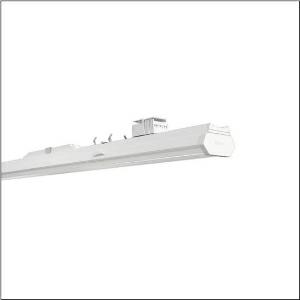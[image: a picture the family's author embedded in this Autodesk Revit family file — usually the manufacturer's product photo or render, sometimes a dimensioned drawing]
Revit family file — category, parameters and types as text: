
# Revit family: licross_11_protected_mo_51tp12dn495g3s4
name_source: partatom
category: Lighting Fixtures
units: mm (PartAtom-declared; Revit-internal decimal feet)

## family parameters
Cut with Voids When Loaded = No
Host = Face
Light Source = No
Part Type = Normal
Room Calculation Point = No
Round Connector Dimension = Use Diameter
Shared = No

## types (1)
- --- (1 x LED, 980 lm, 6.8 W, 4000K)
    Apparent Load = 7 VA
    CIE Flux Codes = 73 92 98 99 100
    Color Rendering = 80
    Color Temperature = 4000K
    Default Elevation = 1800 mm
    Description = Licross 11 Protected MO, luminaire insert, of sheet steel, galvanised, coil coated, white, length: 1.500mm, width: 90mm, height: 101mm, LED rated luminous flux: 9.980lm, light colour: 840, SDCM (Standard Deviation of Colour Matching)MacAdam ≤ 2 SDCM (initial), control gear: DALI 2, with plug, 6-pole, with phase selection, for trunking rail, 9 or 11-core, mains connection: 220..240V, AC, 50/60Hz, rated input power: 61W, for trunking rail, 9-/11-core, internal wiring halogen-free, for emergency light function, converter,control gear: single battery element, battery: LiFePO4, 9Ah, primary light control with lens, of plastic, primary optical cover: cover, of PMMA, light emission: direct distribution, primary light characteristic: symmetric, protection rating (complete): IP64, insulation class (complete): insulation class I (protective earthing), certification: CE, UKCA, protection symbol: D if used in an environment with conductive dust loads with corresponding accessories, impact resistance: IK06, permissible ambient temperature for indoor applications: +5..+35°C, standard: EN 60598-2-22, LABS conformity tested according to VDMA 24364:2018-05, reducing of maximum allowable ambient temperature of 5°C with ceiling mounting, corresponds to IFS (International Featured Standards) requirements for safety and quality in the food industry, The light source and the operating device comply with the requirements of the Ecodesign Regulation (EU) 2019/2020 and are replaceable in accordance with this regulation, packaging unit: 1 piece
    Height = 92 mm
    Lamp = 1 x LED
    Lamp Light Flux = 980 lm
    Lamp Power = 6.8 W
    Lamp count = 1
    Length = 1500 mm
    Luminous efficacy = 144 lm/W
    Manufacturer = Siteco
    ModVariant = No
    Model = 51TP12DN495G3S4
    Mounting Place = Ceiling
    Mounting Type = Pendant
    Number of Poles = 1
    OnlyDefault = Yes
    Power Factor = 1
    Product Name = Licross 11 Protected MO
    Product group = luminaire insert | ceiling pendant
    ProductGroupID = 901
    Protection Class = Protection class I
    Protection Degree = IP 64
    RLX_Detail_Level = 1
    RLX_Emergency_Light_Flux = 0 lm
    RLX_Emergency_Type = 0
    RLX_Emergency_Type_DB = No
    RlxData = <blob elided: 24997 chars, md5=5d90d102>
    Socket = socket
    Standby Power = 0 W
    System Light Flux = 980 lm
    System Power = 7 W
    Type Comments = : emergency light operation: 3 h
    Type Image = l_1256148.jpg
    URL = http://relux.com
    VarID = @adj_094435
    Voltage = 0 V
    Weight = 0.00 kg
    Width = 88 mm

## geometry (parser evidence)
native form markers: Blend x4, Sweep x11
no freeform markers — native parametric forms only
